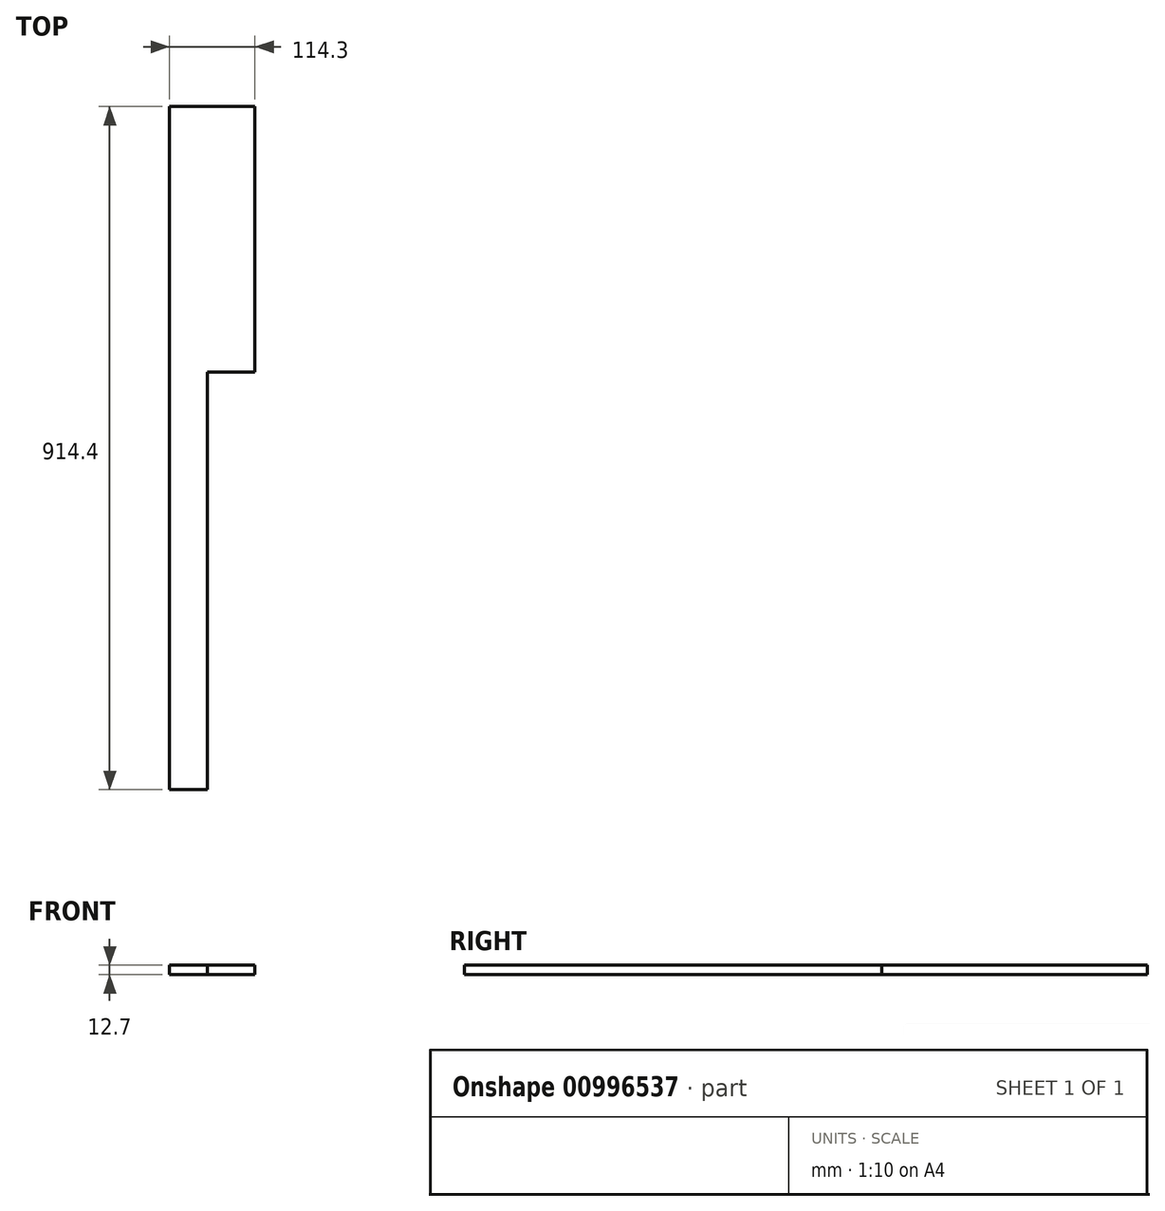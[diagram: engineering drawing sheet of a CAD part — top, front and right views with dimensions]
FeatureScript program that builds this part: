
annotation { "Feature Type Name" : "Feature", "Feature Type Description" : "" }
export const myFeature = defineFeature(function(context is Context, id is Id, definition is map)
    precondition{}
    {
        {
            var Q0;
            Q0=qCreatedBy(makeId("Top.planeOp"),FACE);
            var sketch = newSketch(context, id + "F0", { "sketchPlane" : qUnion([Q0])});
            skLineSegment(sketch, "E0.bottom", {"start": v(0, 661.71) * mm, "end": v(114.3, 661.71) * mm});
            skLineSegment(sketch, "E0.top", {"start": v(0, 306.11) * mm, "end": v(114.3, 306.11) * mm});
            skLineSegment(sketch, "E0.left", {"start": v(0, 661.71) * mm, "end": v(0, 306.11) * mm});
            skLineSegment(sketch, "E0.right", {"start": v(114.3, 661.71) * mm, "end": v(114.3, 306.11) * mm});
            skPoint(sketch, "E1.oppositeSnap0", {"position": v(50.8, 306.11) * mm});
            skLineSegment(sketch, "E1.bottom", {"start": v(0, 306.11) * mm, "end": v(50.8, 306.11) * mm});
            skLineSegment(sketch, "E1.top", {"start": v(0, -252.69) * mm, "end": v(50.8, -252.69) * mm});
            skLineSegment(sketch, "E1.left", {"start": v(0, 306.11) * mm, "end": v(0, -252.69) * mm});
            skLineSegment(sketch, "E1.right", {"start": v(50.8, 306.11) * mm, "end": v(50.8, -252.69) * mm});
            skSolve(sketch);
        }
        {
            var Q0;
            Q0=makeQuery(id+"F0.imprint","IMPRINT",FACE,{"disambiguationData":[TD([[makeQuery(id+"F0.imprint","IMPRINT",EDGE,{"derivedFrom":sQuery(id+"F0.wireOp",EDGE,"E0.bottom")}),-1.0]])]});
            var Q1;
            Q1=makeQuery(id+"F0.imprint","IMPRINT",FACE,{"disambiguationData":[TD([[makeQuery(id+"F0.imprint","IMPRINT",EDGE,{"derivedFrom":sQuery(id+"F0.wireOp",EDGE,"E1.top")}),1.0]])]});
            extrude(context, id + "F1", {"entities" : qUnion([Q0, Q1]), "depth" : 12.7 * mm, "offsetDistance" : 25.4 * mm});
        }
    });
